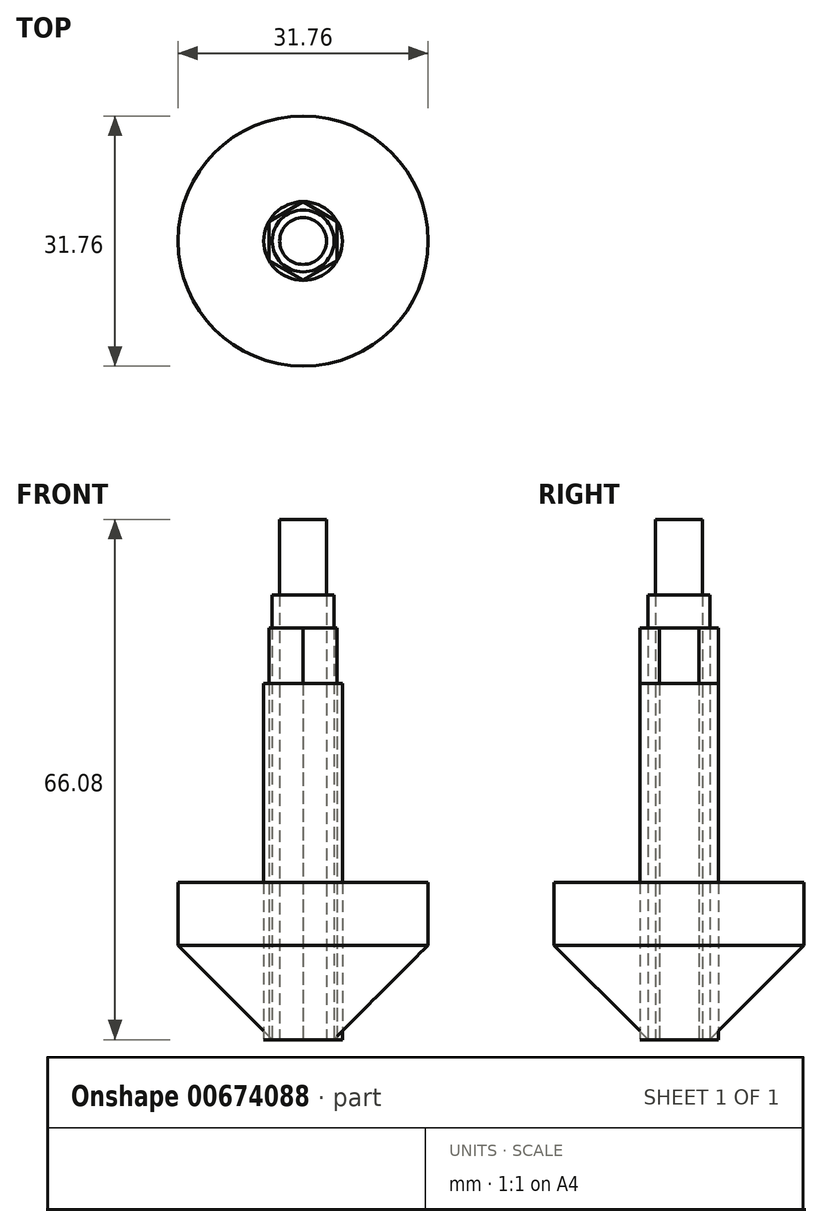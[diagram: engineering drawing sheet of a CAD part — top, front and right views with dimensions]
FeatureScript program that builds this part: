
annotation { "Feature Type Name" : "Feature", "Feature Type Description" : "" }
export const myFeature = defineFeature(function(context is Context, id is Id, definition is map)
    precondition{}
    {
        {
            var Q0;
            Q0=qCreatedBy(makeId("Top.planeOp"),FACE);
            var sketch = newSketch(context, id + "F0", { "sketchPlane" : qUnion([Q0])});
            skCircle(sketch, "E0", {"center": v(0, 0) * mm, "radius": 15.88 * mm});
            skCircle(sketch, "E1", {"center": v(0, 0) * mm, "radius": 10.66 * mm});
            skCircle(sketch, "E2", {"center": v(0, 0) * mm, "radius": 5 * mm});
            skCircle(sketch, "E3.cCircle", {"center": v(0, 0) * mm, "radius": 4.32 * mm, "construction": true});
            skLineSegment(sketch, "E3.0", {"start": v(4.32, 2.5) * mm, "end": v(4.32, -2.5) * mm});
            skLineSegment(sketch, "E3.1", {"start": v(4.32, -2.5) * mm, "end": v(0, -4.99) * mm});
            skLineSegment(sketch, "E3.2", {"start": v(0, -4.99) * mm, "end": v(-4.32, -2.5) * mm});
            skLineSegment(sketch, "E3.3", {"start": v(-4.32, -2.5) * mm, "end": v(-4.32, 2.5) * mm});
            skLineSegment(sketch, "E3.4", {"start": v(-4.32, 2.5) * mm, "end": v(0, 4.99) * mm});
            skLineSegment(sketch, "E3.5", {"start": v(0, 4.99) * mm, "end": v(4.32, 2.5) * mm});
            skPoint(sketch, "E3.0.midPoint", {"position": v(4.32, 0) * mm});
            skCircle(sketch, "E4", {"center": v(0, 0) * mm, "radius": 2.98 * mm});
            skCircle(sketch, "E5", {"center": v(0, 0) * mm, "radius": 3.93 * mm});
            skSolve(sketch);
        }
        {
            var Q0;
            Q0=makeQuery(id+"F0.imprint","IMPRINT",FACE,{"disambiguationData":[TD([[makeQuery(id+"F0.imprint","IMPRINT",EDGE,{"derivedFrom":sQuery(id+"F0.wireOp",EDGE,"E1")}),1.0]])]});
            var Q1;
            {var subQ0=sQuery(id+"F0.wireOp",EDGE,"E3.0");var subQ1=sQuery(id+"F0.wireOp",EDGE,"E2");var subQ2=makeQuery(id+"F0.imprint","INTERSECT",VERTEX,{"disambiguationData":[OD(0.0)],"derivedFrom":[subQ1,subQ0]});Q1=makeQuery(id+"F0.imprint","IMPRINT",FACE,{"disambiguationData":[TD([[makeQuery(id+"F0.imprint","IMPRINT",EDGE,{"disambiguationData":[TD([[subQ2,1.0]])],"derivedFrom":subQ1}),1.0]])]});}
            var Q2;
            Q2=makeQuery(id+"F0.imprint","IMPRINT",FACE,{"disambiguationData":[TD([[makeQuery(id+"F0.imprint","IMPRINT",EDGE,{"derivedFrom":sQuery(id+"F0.wireOp",EDGE,"E5")}),-1.0]])]});
            var Q3;
            Q3=makeQuery(id+"F0.imprint","IMPRINT",FACE,{"disambiguationData":[TD([[makeQuery(id+"F0.imprint","IMPRINT",EDGE,{"derivedFrom":sQuery(id+"F0.wireOp",EDGE,"E4")}),-1.0]])]});
            var Q4;
            Q4=makeQuery(id+"F0.imprint","IMPRINT",FACE,{"disambiguationData":[TD([[makeQuery(id+"F0.imprint","IMPRINT",EDGE,{"derivedFrom":sQuery(id+"F0.wireOp",EDGE,"E4")}),1.0]])]});
            var Q5;
            {var subQ0=sQuery(id+"F0.wireOp",EDGE,"E3.5");var subQ1=sQuery(id+"F0.wireOp",EDGE,"E2");var subQ2=makeQuery(id+"F0.imprint","INTERSECT",VERTEX,{"disambiguationData":[OD(0.0)],"derivedFrom":[subQ1,subQ0]});Q5=makeQuery(id+"F0.imprint","IMPRINT",FACE,{"disambiguationData":[TD([[makeQuery(id+"F0.imprint","IMPRINT",EDGE,{"disambiguationData":[TD([[subQ2,-1.0]])],"derivedFrom":subQ1}),1.0]])]});}
            var Q6;
            {var subQ0=sQuery(id+"F0.wireOp",EDGE,"E3.4");var subQ1=sQuery(id+"F0.wireOp",EDGE,"E2");var subQ2=makeQuery(id+"F0.imprint","INTERSECT",VERTEX,{"disambiguationData":[OD(0.0)],"derivedFrom":[subQ1,subQ0]});Q6=makeQuery(id+"F0.imprint","IMPRINT",FACE,{"disambiguationData":[TD([[makeQuery(id+"F0.imprint","IMPRINT",EDGE,{"disambiguationData":[TD([[subQ2,-1.0]])],"derivedFrom":subQ1}),1.0]])]});}
            var Q7;
            {var subQ0=sQuery(id+"F0.wireOp",EDGE,"E3.3");var subQ1=sQuery(id+"F0.wireOp",EDGE,"E2");var subQ2=makeQuery(id+"F0.imprint","INTERSECT",VERTEX,{"disambiguationData":[OD(0.0)],"derivedFrom":[subQ1,subQ0]});Q7=makeQuery(id+"F0.imprint","IMPRINT",FACE,{"disambiguationData":[TD([[makeQuery(id+"F0.imprint","IMPRINT",EDGE,{"disambiguationData":[TD([[subQ2,-1.0]])],"derivedFrom":subQ1}),1.0]])]});}
            var Q8;
            {var subQ0=sQuery(id+"F0.wireOp",EDGE,"E3.2");var subQ1=sQuery(id+"F0.wireOp",EDGE,"E2");var subQ2=makeQuery(id+"F0.imprint","INTERSECT",VERTEX,{"disambiguationData":[OD(0.0)],"derivedFrom":[subQ1,subQ0]});Q8=makeQuery(id+"F0.imprint","IMPRINT",FACE,{"disambiguationData":[TD([[makeQuery(id+"F0.imprint","IMPRINT",EDGE,{"disambiguationData":[TD([[subQ2,-1.0]])],"derivedFrom":subQ1}),1.0]])]});}
            var Q9;
            {var subQ0=sQuery(id+"F0.wireOp",EDGE,"E3.1");var subQ1=sQuery(id+"F0.wireOp",EDGE,"E2");var subQ2=makeQuery(id+"F0.imprint","INTERSECT",VERTEX,{"disambiguationData":[OD(0.0)],"derivedFrom":[subQ1,subQ0]});Q9=makeQuery(id+"F0.imprint","IMPRINT",FACE,{"disambiguationData":[TD([[makeQuery(id+"F0.imprint","IMPRINT",EDGE,{"disambiguationData":[TD([[subQ2,-1.0]])],"derivedFrom":subQ1}),1.0]])]});}
            var Q10;
            {var subQ0=sQuery(id+"F0.wireOp",EDGE,"E3.5");var subQ1=sQuery(id+"F0.wireOp",EDGE,"E2");var subQ2=makeQuery(id+"F0.imprint","INTERSECT",VERTEX,{"disambiguationData":[OD(0.0)],"derivedFrom":[subQ1,subQ0]});Q10=makeQuery(id+"F0.imprint","IMPRINT",FACE,{"disambiguationData":[TD([[makeQuery(id+"F0.imprint","IMPRINT",EDGE,{"disambiguationData":[TD([[subQ2,1.0]])],"derivedFrom":subQ1}),-1.0]])]});}
            var Q11;
            {var subQ0=sQuery(id+"F0.wireOp",EDGE,"E3.5");var subQ1=sQuery(id+"F0.wireOp",EDGE,"E2");var subQ2=makeQuery(id+"F0.imprint","INTERSECT",VERTEX,{"disambiguationData":[OD(1.0)],"derivedFrom":[subQ1,subQ0]});Q11=makeQuery(id+"F0.imprint","IMPRINT",FACE,{"disambiguationData":[TD([[makeQuery(id+"F0.imprint","IMPRINT",EDGE,{"disambiguationData":[TD([[subQ2,-1.0]])],"derivedFrom":subQ1}),-1.0]])]});}
            var Q12;
            {var subQ0=sQuery(id+"F0.wireOp",EDGE,"E3.4");var subQ1=sQuery(id+"F0.wireOp",EDGE,"E2");var subQ2=makeQuery(id+"F0.imprint","INTERSECT",VERTEX,{"disambiguationData":[OD(1.0)],"derivedFrom":[subQ1,subQ0]});Q12=makeQuery(id+"F0.imprint","IMPRINT",FACE,{"disambiguationData":[TD([[makeQuery(id+"F0.imprint","IMPRINT",EDGE,{"disambiguationData":[TD([[subQ2,-1.0]])],"derivedFrom":subQ1}),-1.0]])]});}
            var Q13;
            {var subQ0=sQuery(id+"F0.wireOp",EDGE,"E3.3");var subQ1=sQuery(id+"F0.wireOp",EDGE,"E2");var subQ2=makeQuery(id+"F0.imprint","INTERSECT",VERTEX,{"disambiguationData":[OD(1.0)],"derivedFrom":[subQ1,subQ0]});Q13=makeQuery(id+"F0.imprint","IMPRINT",FACE,{"disambiguationData":[TD([[makeQuery(id+"F0.imprint","IMPRINT",EDGE,{"disambiguationData":[TD([[subQ2,-1.0]])],"derivedFrom":subQ1}),-1.0]])]});}
            var Q14;
            {var subQ0=sQuery(id+"F0.wireOp",EDGE,"E3.2");var subQ1=sQuery(id+"F0.wireOp",EDGE,"E2");var subQ2=makeQuery(id+"F0.imprint","INTERSECT",VERTEX,{"disambiguationData":[OD(1.0)],"derivedFrom":[subQ1,subQ0]});Q14=makeQuery(id+"F0.imprint","IMPRINT",FACE,{"disambiguationData":[TD([[makeQuery(id+"F0.imprint","IMPRINT",EDGE,{"disambiguationData":[TD([[subQ2,-1.0]])],"derivedFrom":subQ1}),-1.0]])]});}
            var Q15;
            {var subQ0=sQuery(id+"F0.wireOp",EDGE,"E3.1");var subQ1=sQuery(id+"F0.wireOp",EDGE,"E2");var subQ2=makeQuery(id+"F0.imprint","INTERSECT",VERTEX,{"disambiguationData":[OD(1.0)],"derivedFrom":[subQ1,subQ0]});Q15=makeQuery(id+"F0.imprint","IMPRINT",FACE,{"disambiguationData":[TD([[makeQuery(id+"F0.imprint","IMPRINT",EDGE,{"disambiguationData":[TD([[subQ2,-1.0]])],"derivedFrom":subQ1}),-1.0]])]});}
            var Q16;
            Q16=makeQuery(id+"F0.imprint","IMPRINT",FACE,{"disambiguationData":[TD([[makeQuery(id+"F0.imprint","IMPRINT",EDGE,{"derivedFrom":sQuery(id+"F0.wireOp",EDGE,"E0")}),1.0]])]});
            extrude(context, id + "F1", {"entities" : qUnion([Q0, Q1, Q2, Q3, Q4, Q5, Q6, Q7, Q8, Q9, Q10, Q11, Q12, Q13, Q14, Q15, Q16]), "depth" : 20 * mm, "offsetDistance" : 25 * mm});
        }
        {
            var Q0;
            Q0=makeQuery(id+"F0.imprint","IMPRINT",FACE,{"disambiguationData":[TD([[makeQuery(id+"F0.imprint","IMPRINT",EDGE,{"derivedFrom":sQuery(id+"F0.wireOp",EDGE,"E5")}),-1.0]])]});
            var Q1;
            {var subQ0=sQuery(id+"F0.wireOp",EDGE,"E3.3");var subQ1=sQuery(id+"F0.wireOp",EDGE,"E2");var subQ2=makeQuery(id+"F0.imprint","INTERSECT",VERTEX,{"disambiguationData":[OD(0.0)],"derivedFrom":[subQ1,subQ0]});Q1=makeQuery(id+"F0.imprint","IMPRINT",FACE,{"disambiguationData":[TD([[makeQuery(id+"F0.imprint","IMPRINT",EDGE,{"disambiguationData":[TD([[subQ2,-1.0]])],"derivedFrom":subQ1}),1.0]])]});}
            var Q2;
            {var subQ0=sQuery(id+"F0.wireOp",EDGE,"E3.4");var subQ1=sQuery(id+"F0.wireOp",EDGE,"E2");var subQ2=makeQuery(id+"F0.imprint","INTERSECT",VERTEX,{"disambiguationData":[OD(0.0)],"derivedFrom":[subQ1,subQ0]});Q2=makeQuery(id+"F0.imprint","IMPRINT",FACE,{"disambiguationData":[TD([[makeQuery(id+"F0.imprint","IMPRINT",EDGE,{"disambiguationData":[TD([[subQ2,-1.0]])],"derivedFrom":subQ1}),1.0]])]});}
            var Q3;
            {var subQ0=sQuery(id+"F0.wireOp",EDGE,"E3.0");var subQ1=sQuery(id+"F0.wireOp",EDGE,"E2");var subQ2=makeQuery(id+"F0.imprint","INTERSECT",VERTEX,{"disambiguationData":[OD(0.0)],"derivedFrom":[subQ1,subQ0]});Q3=makeQuery(id+"F0.imprint","IMPRINT",FACE,{"disambiguationData":[TD([[makeQuery(id+"F0.imprint","IMPRINT",EDGE,{"disambiguationData":[TD([[subQ2,1.0]])],"derivedFrom":subQ1}),1.0]])]});}
            var Q4;
            Q4=makeQuery(id+"F0.imprint","IMPRINT",FACE,{"disambiguationData":[TD([[makeQuery(id+"F0.imprint","IMPRINT",EDGE,{"derivedFrom":sQuery(id+"F0.wireOp",EDGE,"E4")}),-1.0]])]});
            var Q5;
            {var subQ0=sQuery(id+"F0.wireOp",EDGE,"E3.5");var subQ1=sQuery(id+"F0.wireOp",EDGE,"E2");var subQ2=makeQuery(id+"F0.imprint","INTERSECT",VERTEX,{"disambiguationData":[OD(0.0)],"derivedFrom":[subQ1,subQ0]});Q5=makeQuery(id+"F0.imprint","IMPRINT",FACE,{"disambiguationData":[TD([[makeQuery(id+"F0.imprint","IMPRINT",EDGE,{"disambiguationData":[TD([[subQ2,-1.0]])],"derivedFrom":subQ1}),1.0]])]});}
            var Q6;
            {var subQ0=sQuery(id+"F0.wireOp",EDGE,"E3.2");var subQ1=sQuery(id+"F0.wireOp",EDGE,"E2");var subQ2=makeQuery(id+"F0.imprint","INTERSECT",VERTEX,{"disambiguationData":[OD(0.0)],"derivedFrom":[subQ1,subQ0]});Q6=makeQuery(id+"F0.imprint","IMPRINT",FACE,{"disambiguationData":[TD([[makeQuery(id+"F0.imprint","IMPRINT",EDGE,{"disambiguationData":[TD([[subQ2,-1.0]])],"derivedFrom":subQ1}),1.0]])]});}
            var Q7;
            {var subQ0=sQuery(id+"F0.wireOp",EDGE,"E3.1");var subQ1=sQuery(id+"F0.wireOp",EDGE,"E2");var subQ2=makeQuery(id+"F0.imprint","INTERSECT",VERTEX,{"disambiguationData":[OD(0.0)],"derivedFrom":[subQ1,subQ0]});Q7=makeQuery(id+"F0.imprint","IMPRINT",FACE,{"disambiguationData":[TD([[makeQuery(id+"F0.imprint","IMPRINT",EDGE,{"disambiguationData":[TD([[subQ2,-1.0]])],"derivedFrom":subQ1}),1.0]])]});}
            var Q8;
            Q8=makeQuery(id+"F0.imprint","IMPRINT",FACE,{"disambiguationData":[TD([[makeQuery(id+"F0.imprint","IMPRINT",EDGE,{"derivedFrom":sQuery(id+"F0.wireOp",EDGE,"E4")}),1.0]])]});
            extrude(context, id + "F2", {"entities" : qUnion([Q0, Q1, Q2, Q3, Q4, Q5, Q6, Q7, Q8]), "depth" : (20 + 25.24) * mm, "offsetDistance" : 25 * mm});
        }
        {
            var Q0;
            Q0=makeQuery(id+"F0.imprint","IMPRINT",FACE,{"disambiguationData":[TD([[makeQuery(id+"F0.imprint","IMPRINT",EDGE,{"derivedFrom":sQuery(id+"F0.wireOp",EDGE,"E4")}),-1.0]])]});
            var Q1;
            Q1=makeQuery(id+"F0.imprint","IMPRINT",FACE,{"disambiguationData":[TD([[makeQuery(id+"F0.imprint","IMPRINT",EDGE,{"derivedFrom":sQuery(id+"F0.wireOp",EDGE,"E5")}),-1.0]])]});
            var Q2;
            Q2=makeQuery(id+"F0.imprint","IMPRINT",FACE,{"disambiguationData":[TD([[makeQuery(id+"F0.imprint","IMPRINT",EDGE,{"derivedFrom":sQuery(id+"F0.wireOp",EDGE,"E4")}),1.0]])]});
            extrude(context, id + "F3", {"entities" : qUnion([Q0, Q1, Q2]), "depth" : 52.33 * mm, "offsetDistance" : 25 * mm});
        }
        {
            var Q0;
            Q0=makeQuery(id+"F0.imprint","IMPRINT",FACE,{"disambiguationData":[TD([[makeQuery(id+"F0.imprint","IMPRINT",EDGE,{"derivedFrom":sQuery(id+"F0.wireOp",EDGE,"E4")}),-1.0]])]});
            var Q1;
            Q1=makeQuery(id+"F0.imprint","IMPRINT",FACE,{"disambiguationData":[TD([[makeQuery(id+"F0.imprint","IMPRINT",EDGE,{"derivedFrom":sQuery(id+"F0.wireOp",EDGE,"E4")}),1.0]])]});
            extrude(context, id + "F4", {"entities" : qUnion([Q0, Q1]), "depth" : (66.5 - 10) * mm, "offsetDistance" : 25 * mm});
        }
        {
            var Q0;
            Q0=makeQuery(id+"F0.imprint","IMPRINT",FACE,{"disambiguationData":[TD([[makeQuery(id+"F0.imprint","IMPRINT",EDGE,{"derivedFrom":sQuery(id+"F0.wireOp",EDGE,"E4")}),1.0]])]});
            extrude(context, id + "F5", {"entities" : qUnion([Q0]), "depth" : 66.08 * mm, "offsetDistance" : 25 * mm});
        }
        {
            var Q0;
            Q0=makeQuery(id+"F1.opExtrude","CAP_FACE",FACE,{"disambiguationData":[OSD([sQuery(id+"F0.wireOp",EDGE,"E0")])],"isStart":false});
            var sketch = newSketch(context, id + "F6", { "sketchPlane" : qUnion([Q0])});
            skCircle(sketch, "E6", {"center": v(0, 0) * mm, "radius": 30 * mm});
            skSolve(sketch);
        }
        {
            var Q0;
            Q0=makeQuery(id+"F1.opExtrude","CAP_EDGE",EDGE,{"disambiguationData":[OSD([sQuery(id+"F0.wireOp",EDGE,"E0")])],"isStart":true});
            chamfer(context, id + "F7", {"entities" : qUnion([Q0]), "width" : 12 * mm, "tangentPropagation" : true});
        }
    });
